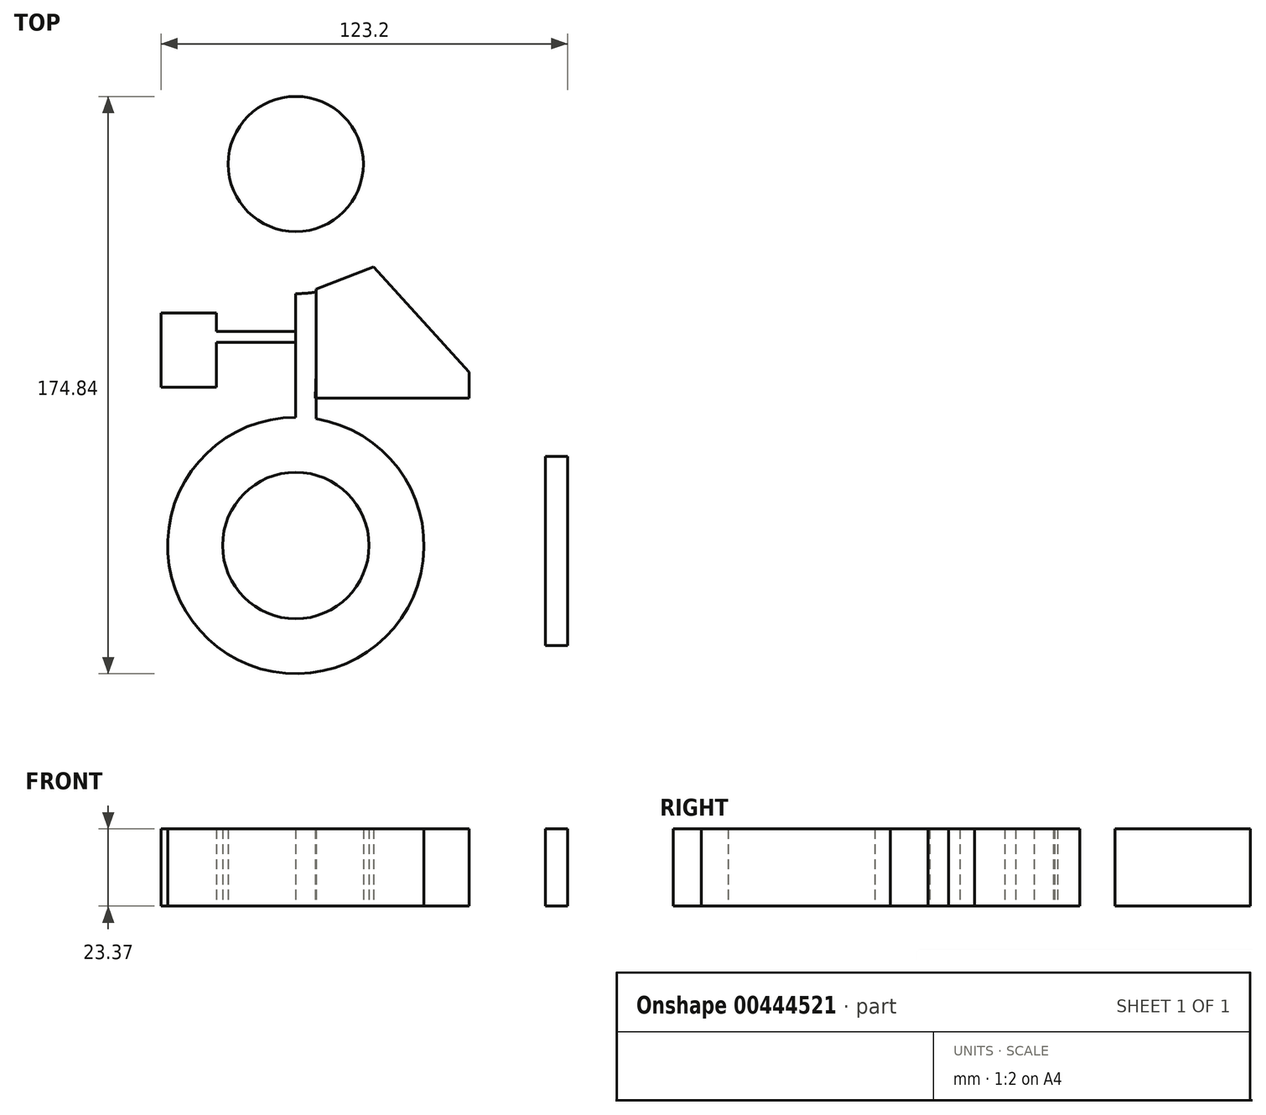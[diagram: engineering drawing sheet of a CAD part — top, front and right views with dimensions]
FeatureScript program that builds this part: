
annotation { "Feature Type Name" : "Feature", "Feature Type Description" : "" }
export const myFeature = defineFeature(function(context is Context, id is Id, definition is map)
    precondition{}
    {
        {
            var Q0;
            Q0=qCreatedBy(makeId("Top.planeOp"),FACE);
            var sketch = newSketch(context, id + "F0", { "sketchPlane" : qUnion([Q0])});
            skCircle(sketch, "E0", {"center": v(0, 0) * mm, "radius": 38.84 * mm});
            skLineSegment(sketch, "E1", {"start": v(0, 38.84) * mm, "end": v(0, 57.56) * mm});
            skLineSegment(sketch, "E2", {"start": v(0, 57.56) * mm, "end": v(6.16, 57.56) * mm});
            skLineSegment(sketch, "E3", {"start": v(6.16, 57.56) * mm, "end": v(6.16, 38.35) * mm});
            skLineSegment(sketch, "E4.MirrorCS", {"start": v(6.16, 57.56) * mm, "end": v(6.16, 76.76) * mm});
            skLineSegment(sketch, "E5.MirrorCS", {"start": v(0, 76.27) * mm, "end": v(0, 57.56) * mm});
            skCircle(sketch, "E6.MirrorC", {"center": v(0, 115.11) * mm, "radius": 38.84 * mm});
            skSolve(sketch);
        }
        {
            var Q0;
            Q0=makeQuery(id+"F0.imprint","IMPRINT",FACE,{"disambiguationData":[TD([[makeQuery(id+"F0.imprint","IMPRINT",EDGE,{"derivedFrom":sQuery(id+"F0.wireOp",EDGE,"E2")}),-1.0]])]});
            var sketch = newSketch(context, id + "F1", { "sketchPlane" : qUnion([Q0])});
            skLineSegment(sketch, "E7", {"start": v(6.16, 52.5) * mm, "end": v(52.5, 52.5) * mm});
            skLineSegment(sketch, "E8", {"start": v(52.5, 52.5) * mm, "end": v(52.5, 44.62) * mm});
            skLineSegment(sketch, "E9", {"start": v(52.5, 44.62) * mm, "end": v(5.95, 44.62) * mm});
            skLineSegment(sketch, "E10", {"start": v(5.95, 44.62) * mm, "end": v(6.16, 52.5) * mm});
            skCircle(sketch, "E11", {"center": v(0, 0) * mm, "radius": 22.18 * mm});
            skCircle(sketch, "E12", {"center": v(0, 115.53) * mm, "radius": 20.47 * mm});
            skLineSegment(sketch, "E13", {"start": v(22.18, 0) * mm, "end": v(82.4, 0) * mm});
            skLineSegment(sketch, "E14", {"start": v(82.4, 0) * mm, "end": v(82.4, -30.3) * mm});
            skLineSegment(sketch, "E15", {"start": v(82.4, -30.3) * mm, "end": v(82.4, 0) * mm});
            skLineSegment(sketch, "E16", {"start": v(82.4, 0) * mm, "end": v(82.4, 26.95) * mm});
            skLineSegment(sketch, "E17", {"start": v(82.4, 26.95) * mm, "end": v(75.67, 26.95) * mm});
            skLineSegment(sketch, "E18", {"start": v(75.67, 26.95) * mm, "end": v(75.67, 0) * mm});
            skLineSegment(sketch, "E19", {"start": v(75.67, 0) * mm, "end": v(82.4, 0) * mm});
            skLineSegment(sketch, "E20", {"start": v(82.4, -30.3) * mm, "end": v(75.67, -30.3) * mm});
            skLineSegment(sketch, "E21", {"start": v(75.67, -30.3) * mm, "end": v(75.67, 0) * mm});
            skLineSegment(sketch, "E22", {"start": v(0, 64.88) * mm, "end": v(-24.03, 64.88) * mm});
            skLineSegment(sketch, "E23", {"start": v(-24.03, 64.88) * mm, "end": v(-24.03, 61.56) * mm});
            skLineSegment(sketch, "E24", {"start": v(-24.03, 61.56) * mm, "end": v(0, 61.56) * mm});
            skLineSegment(sketch, "E25", {"start": v(0, 61.56) * mm, "end": v(0, 64.88) * mm});
            skLineSegment(sketch, "E26", {"start": v(-24.03, 61.56) * mm, "end": v(-24.03, 47.96) * mm});
            skLineSegment(sketch, "E27", {"start": v(-24.03, 47.96) * mm, "end": v(-40.8, 47.96) * mm});
            skLineSegment(sketch, "E28", {"start": v(-40.8, 47.96) * mm, "end": v(-40.8, 70.48) * mm});
            skLineSegment(sketch, "E29", {"start": v(-40.8, 70.48) * mm, "end": v(-24.03, 70.48) * mm});
            skLineSegment(sketch, "E30", {"start": v(-24.03, 70.48) * mm, "end": v(-24.03, 64.88) * mm});
            skLineSegment(sketch, "E31", {"start": v(52.5, 52.5) * mm, "end": v(23.57, 84.4) * mm});
            skLineSegment(sketch, "E32", {"start": v(6.16, 52.5) * mm, "end": v(6.16, 77.6) * mm});
            skLineSegment(sketch, "E33", {"start": v(6.16, 77.6) * mm, "end": v(23.57, 84.4) * mm});
            skSolve(sketch);
        }
        {
            var Q0;
            Q0 = qSketchRegion(id + "F1", true);
            var Q1;
            Q1=makeQuery(id+"F0.imprint","IMPRINT",FACE,{"disambiguationData":[TD([[makeQuery(id+"F0.imprint","IMPRINT",EDGE,{"derivedFrom":sQuery(id+"F0.wireOp",EDGE,"E2")}),-1.0]])]});
            var Q2;
            Q2=makeQuery(id+"F0.imprint","IMPRINT",FACE,{"disambiguationData":[TD([[makeQuery(id+"F0.imprint","IMPRINT",EDGE,{"derivedFrom":sQuery(id+"F0.wireOp",EDGE,"E2")}),1.0]])]});
            var Q3;
            {var subQ0=sQuery(id+"F0.wireOp",EDGE,"E6.MirrorC");var subQ1=makeQuery(id+"F0.imprint","INTERSECT",VERTEX,{"derivedFrom":[subQ0,sQuery(id+"F0.wireOp",EDGE,"E5.MirrorCS")]});Q3=makeQuery(id+"F0.imprint","IMPRINT",FACE,{"disambiguationData":[TD([[makeQuery(id+"F0.imprint","IMPRINT",EDGE,{"disambiguationData":[TD([[subQ1,1.0]])],"derivedFrom":subQ0}),-1.0]])]});}
            var Q4;
            {var subQ0=sQuery(id+"F0.wireOp",EDGE,"E0");var subQ1=makeQuery(id+"F0.imprint","INTERSECT",VERTEX,{"derivedFrom":[subQ0,sQuery(id+"F0.wireOp",EDGE,"E1")]});Q4=makeQuery(id+"F0.imprint","IMPRINT",FACE,{"disambiguationData":[TD([[makeQuery(id+"F0.imprint","IMPRINT",EDGE,{"disambiguationData":[TD([[subQ1,1.0]])],"derivedFrom":subQ0}),1.0]])]});}
            extrude(context, id + "F2", {"entities" : qUnion([Q0, Q1, Q2, Q3, Q4]), "depth" : 23.37 * mm});
        }
    });
